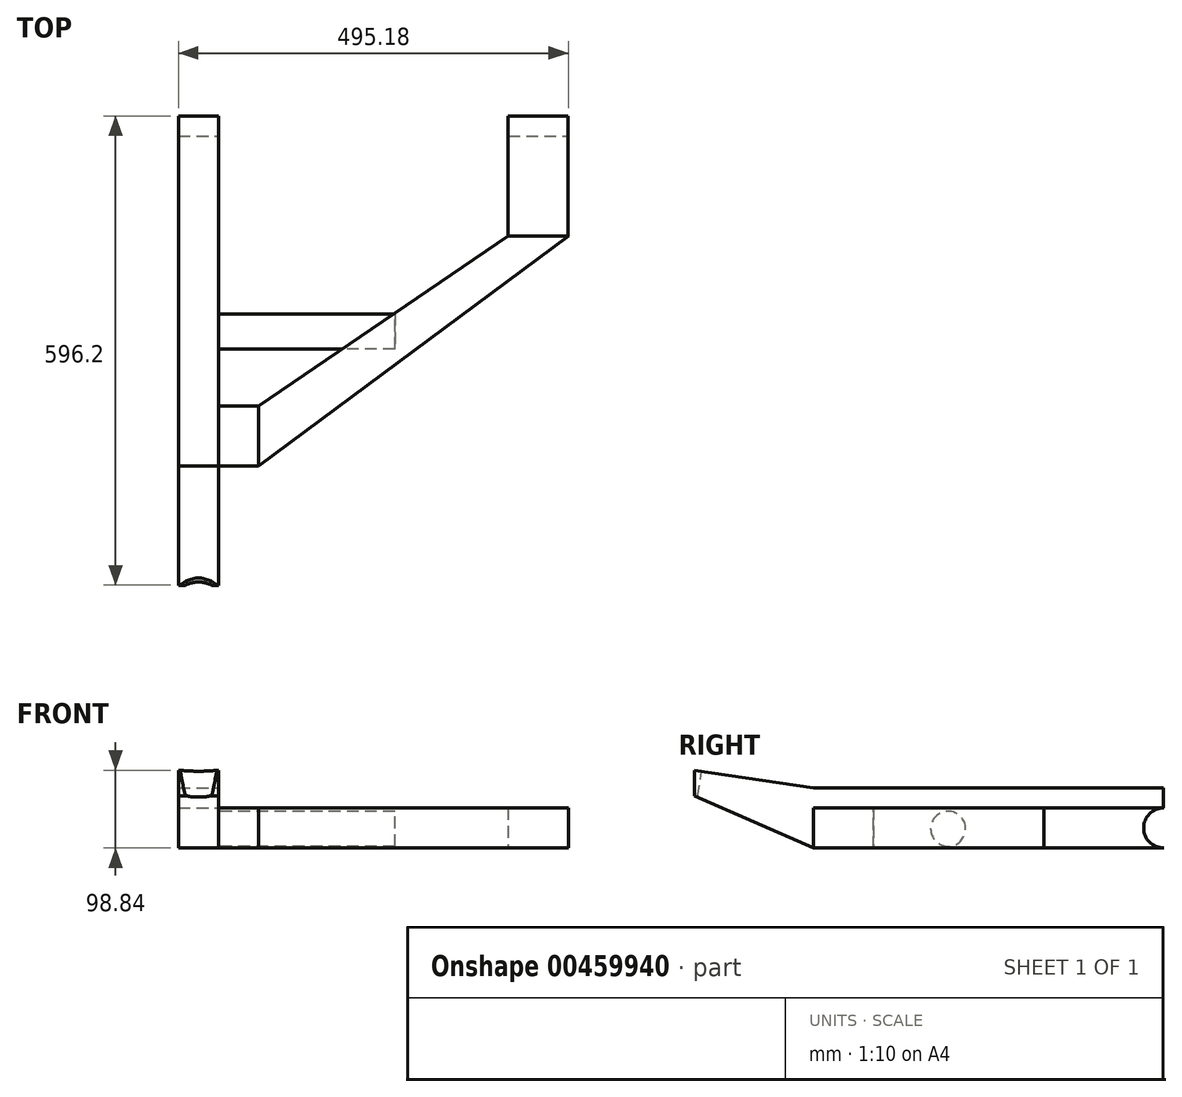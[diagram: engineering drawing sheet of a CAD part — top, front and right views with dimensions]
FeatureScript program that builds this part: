
annotation { "Feature Type Name" : "Feature", "Feature Type Description" : "" }
export const myFeature = defineFeature(function(context is Context, id is Id, definition is map)
    precondition{}
    {
        {
            var Q0;
            Q0=qCreatedBy(makeId("Top.planeOp"),FACE);
            var sketch = newSketch(context, id + "F0", { "sketchPlane" : qUnion([Q0])});
            skLineSegment(sketch, "E0.bottom", {"start": v(-50.8, 550.56) * mm, "end": v(0, 550.56) * mm});
            skLineSegment(sketch, "E1", {"start": v(0, 550.56) * mm, "end": v(0, 184.56) * mm});
            skLineSegment(sketch, "E2", {"start": v(0, 184.56) * mm, "end": v(0, 106.06) * mm});
            skLineSegment(sketch, "E3", {"start": v(0, 106.06) * mm, "end": v(-50.8, 106.06) * mm});
            skLineSegment(sketch, "E4", {"start": v(-50.8, 550.56) * mm, "end": v(-50.8, 106.06) * mm});
            skSolve(sketch);
        }
        {
            var Q0;
            Q0=makeQuery(id+"F0.imprint","IMPRINT",FACE,{"disambiguationData":[TD([[makeQuery(id+"F0.imprint","IMPRINT",EDGE,{"derivedFrom":sQuery(id+"F0.wireOp",EDGE,"E0.bottom")}),-1.0]])]});
            extrude(context, id + "F1", {"entities" : qUnion([Q0]), "depth" : 76.2 * mm});
        }
        {
            var Q0;
            Q0=makeQuery(id+"F1.opExtrude","SWEPT_FACE",FACE,{"disambiguationData":[OSD([sQuery(id+"F0.wireOp",EDGE,"E4")])]});
            var sketch = newSketch(context, id + "F2", { "sketchPlane" : qUnion([Q0])});
            skLineSegment(sketch, "E5", {"start": v(-106.06, 76.2) * mm, "end": v(45.5, 98.84) * mm});
            skLineSegment(sketch, "E6", {"start": v(45.5, 98.84) * mm, "end": v(45.5, 66.44) * mm});
            skLineSegment(sketch, "E7", {"start": v(45.5, 66.44) * mm, "end": v(-106.06, 0) * mm});
            skLineSegment(sketch, "E8", {"start": v(-106.06, 0) * mm, "end": v(-106.06, 76.2) * mm});
            skSolve(sketch);
        }
        {
            var Q0;
            Q0=makeQuery(id+"F2.imprint","IMPRINT",FACE,{"disambiguationData":[TD([[makeQuery(id+"F2.imprint","IMPRINT",EDGE,{"derivedFrom":sQuery(id+"F2.wireOp",EDGE,"E5")}),-1.0]])]});
            extrude(context, id + "F3", {"entities" : qUnion([Q0]), "operationType" : NewBodyOperationType.ADD, "oppositeDirection" : true, "depth" : 50.8 * mm});
        }
        {
            var Q0;
            Q0=makeQuery(id+"F3.opExtrude","SWEPT_FACE",FACE,{"disambiguationData":[OSD([sQuery(id+"F2.wireOp",EDGE,"E5")])]});
            var sketch = newSketch(context, id + "F4", { "sketchPlane" : qUnion([Q0])});
            skCircle(sketch, "E9", {"center": v(-25.4, -84.3) * mm, "radius": 34.28 * mm});
            skSolve(sketch);
        }
        {
            var Q0;
            Q0=sQuery(id+"F4.wireOp",VERTEX,"E9.center");
            var Q1;
            Q1=makeQuery(id+"F1.opExtrude","SWEPT_BODY",BODY,{"disambiguationData":[OSD([sQuery(id+"F0.wireOp",EDGE,"E0.bottom"),sQuery(id+"F0.wireOp",EDGE,"E1"),sQuery(id+"F0.wireOp",EDGE,"E2"),sQuery(id+"F0.wireOp",EDGE,"E3"),sQuery(id+"F0.wireOp",EDGE,"E4")])]});
            hole(context, id + "F5", {"style" : HoleStyle.SIMPLE, "endStyle" : HoleEndStyle.THROUGH, "holeDiameter" : 67.7 * mm, "isTappedThrough" : true, "tappedDepth" : 12.7 * mm, "tapClearance" : 3, "locations" : qUnion([Q0]), "scope" : qUnion([Q1])});
        }
        {
            var Q0;
            Q0=makeQuery(id+"F3.boolean.opBoolean","MERGE",FACE,{"derivedFrom":[makeQuery(id+"F1.opExtrude","SWEPT_FACE",FACE,{"disambiguationData":[OSD([sQuery(id+"F0.wireOp",EDGE,"E1"),sQuery(id+"F0.wireOp",EDGE,"E2")])]}),makeQuery(id+"F3.opExtrude","CAP_FACE",FACE,{"disambiguationData":[OSD([sQuery(id+"F2.wireOp",EDGE,"E5"),sQuery(id+"F2.wireOp",EDGE,"E6"),sQuery(id+"F2.wireOp",EDGE,"E7"),sQuery(id+"F2.wireOp",EDGE,"E8")])],"isStart":false})]});
            var sketch = newSketch(context, id + "F6", { "sketchPlane" : qUnion([Q0])});
            skLineSegment(sketch, "E10.bottom", {"start": v(106.06, 0) * mm, "end": v(182.26, 0) * mm});
            skLineSegment(sketch, "E10.top", {"start": v(106.06, 50.8) * mm, "end": v(182.26, 50.8) * mm});
            skLineSegment(sketch, "E10.left", {"start": v(106.06, 0) * mm, "end": v(106.06, 50.8) * mm});
            skLineSegment(sketch, "E10.right", {"start": v(182.26, 0) * mm, "end": v(182.26, 50.8) * mm});
            skSolve(sketch);
        }
        {
            var Q0;
            Q0=makeQuery(id+"F6.imprint","IMPRINT",FACE,{"disambiguationData":[TD([[makeQuery(id+"F6.imprint","IMPRINT",EDGE,{"derivedFrom":sQuery(id+"F6.wireOp",EDGE,"E10.bottom")}),-1.0]])]});
            extrude(context, id + "F7", {"entities" : qUnion([Q0]), "operationType" : NewBodyOperationType.ADD, "depth" : 50.8 * mm});
        }
        {
            var Q0;
            Q0=qCreatedBy(makeId("Top.planeOp"),FACE);
            var sketch = newSketch(context, id + "F8", { "sketchPlane" : qUnion([Q0])});
            skLineSegment(sketch, "E11", {"start": v(-25.8, 550.7) * mm, "end": v(406, 550.7) * mm});
            skLineSegment(sketch, "E12.bottom", {"start": v(367.9, 550.7) * mm, "end": v(444.1, 550.7) * mm});
            skLineSegment(sketch, "E12.top", {"start": v(367.9, 398.3) * mm, "end": v(444.1, 398.3) * mm});
            skLineSegment(sketch, "E12.left", {"start": v(367.9, 550.7) * mm, "end": v(367.9, 398.3) * mm});
            skLineSegment(sketch, "E12.right", {"start": v(444.1, 550.7) * mm, "end": v(444.1, 398.3) * mm});
            skSolve(sketch);
        }
        {
            var Q0;
            Q0=makeQuery(id+"F8.imprint","IMPRINT",FACE,{"disambiguationData":[TD([[makeQuery(id+"F8.imprint","IMPRINT",EDGE,{"derivedFrom":sQuery(id+"F8.wireOp",EDGE,"E12.top")}),1.0]])]});
            extrude(context, id + "F9", {"entities" : qUnion([Q0]), "depth" : 50.8 * mm});
        }
        {
            var Q0;
            Q0=qCreatedBy(makeId("Top.planeOp"),FACE);
            var sketch = newSketch(context, id + "F10", { "sketchPlane" : qUnion([Q0])});
            skLineSegment(sketch, "E13", {"start": v(50.77, 182.22) * mm, "end": v(367.87, 398.34) * mm});
            skLineSegment(sketch, "E14", {"start": v(367.87, 398.34) * mm, "end": v(444.38, 398.34) * mm});
            skLineSegment(sketch, "E15", {"start": v(444.38, 398.34) * mm, "end": v(50.72, 106.08) * mm});
            skLineSegment(sketch, "E16", {"start": v(50.72, 106.08) * mm, "end": v(50.77, 182.22) * mm});
            skSolve(sketch);
        }
        {
            var Q0;
            Q0=makeQuery(id+"F10.imprint","IMPRINT",FACE,{"disambiguationData":[TD([[makeQuery(id+"F10.imprint","IMPRINT",EDGE,{"derivedFrom":sQuery(id+"F10.wireOp",EDGE,"E13")}),-1.0]])]});
            extrude(context, id + "F11", {"entities" : qUnion([Q0]), "depth" : 50.8 * mm});
        }
        {
            var Q0;
            Q0=makeQuery(id+"F9.opExtrude","SWEPT_FACE",FACE,{"disambiguationData":[OSD([sQuery(id+"F8.wireOp",EDGE,"E12.right")])]});
            var sketch = newSketch(context, id + "F12", { "sketchPlane" : qUnion([Q0])});
            skCircle(sketch, "E17", {"center": v(550.7, 25.4) * mm, "radius": 25.4 * mm});
            skSolve(sketch);
        }
        {
            var Q0;
            Q0=sQuery(id+"F12.wireOp",VERTEX,"E17.center");
            var Q1;
            Q1=makeQuery(id+"F1.opExtrude","SWEPT_BODY",BODY,{"disambiguationData":[OSD([sQuery(id+"F0.wireOp",EDGE,"E0.bottom"),sQuery(id+"F0.wireOp",EDGE,"E1"),sQuery(id+"F0.wireOp",EDGE,"E2"),sQuery(id+"F0.wireOp",EDGE,"E3"),sQuery(id+"F0.wireOp",EDGE,"E4")])]});
            var Q2;
            Q2=makeQuery(id+"F9.opExtrude","SWEPT_BODY",BODY,{"disambiguationData":[OSD([sQuery(id+"F8.wireOp",EDGE,"E12.bottom"),sQuery(id+"F8.wireOp",EDGE,"E12.top"),sQuery(id+"F8.wireOp",EDGE,"E12.left"),sQuery(id+"F8.wireOp",EDGE,"E12.right")])]});
            hole(context, id + "F13", {"style" : HoleStyle.SIMPLE, "endStyle" : HoleEndStyle.THROUGH, "holeDiameter" : 50.8 * mm, "isTappedThrough" : true, "tappedDepth" : 12.7 * mm, "tapClearance" : 3, "locations" : qUnion([Q0]), "scope" : qUnion([Q1, Q2])});
        }
        {
            var Q0;
            Q0=makeQuery(id+"F3.boolean.opBoolean","MERGE",FACE,{"derivedFrom":[makeQuery(id+"F1.opExtrude","SWEPT_FACE",FACE,{"disambiguationData":[OSD([sQuery(id+"F0.wireOp",EDGE,"E1"),sQuery(id+"F0.wireOp",EDGE,"E2")])]}),makeQuery(id+"F3.opExtrude","CAP_FACE",FACE,{"disambiguationData":[OSD([sQuery(id+"F2.wireOp",EDGE,"E5"),sQuery(id+"F2.wireOp",EDGE,"E6"),sQuery(id+"F2.wireOp",EDGE,"E7"),sQuery(id+"F2.wireOp",EDGE,"E8")])],"isStart":false})]});
            var sketch = newSketch(context, id + "F14", { "sketchPlane" : qUnion([Q0])});
            skCircle(sketch, "E18", {"center": v(276.92, 24.38) * mm, "radius": 22.23 * mm});
            skSolve(sketch);
        }
        {
            var Q0;
            Q0=makeQuery(id+"F14.imprint","IMPRINT",FACE,{"disambiguationData":[TD([[makeQuery(id+"F14.imprint","IMPRINT",EDGE,{"derivedFrom":sQuery(id+"F14.wireOp",EDGE,"E18")}),1.0]])]});
            extrude(context, id + "F15", {"entities" : qUnion([Q0]), "depth" : 224.03 * mm});
        }
    });
